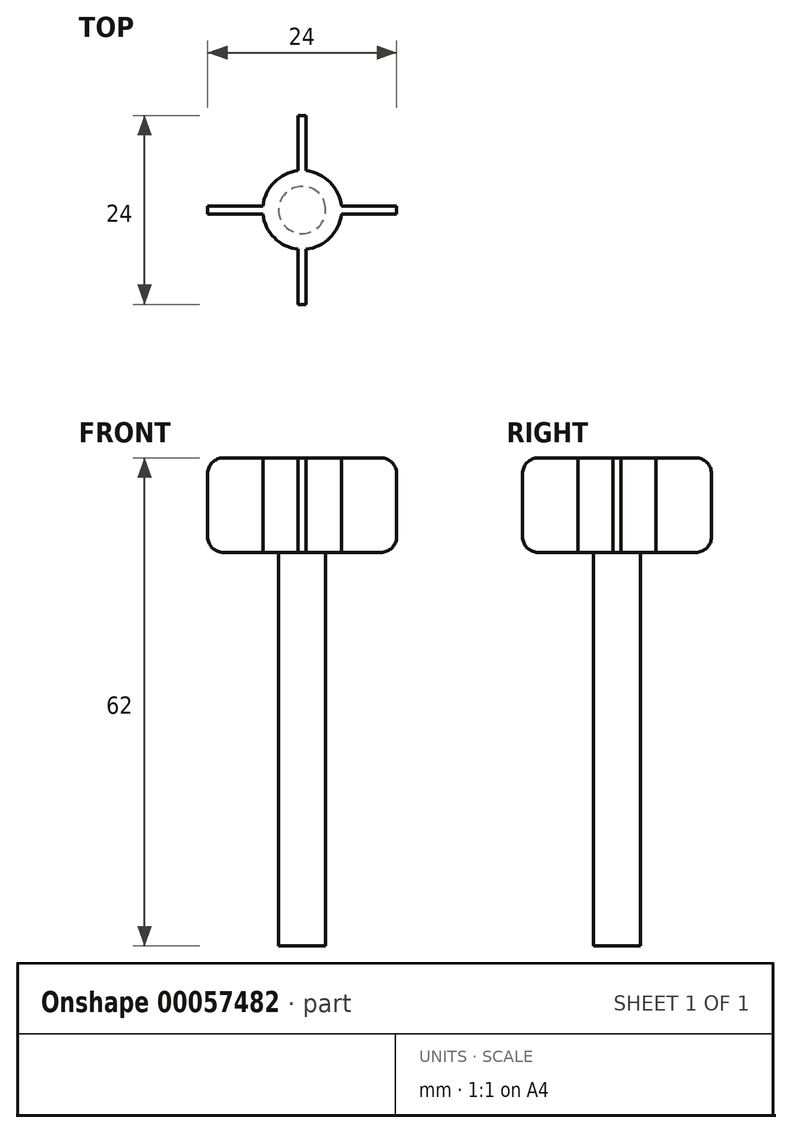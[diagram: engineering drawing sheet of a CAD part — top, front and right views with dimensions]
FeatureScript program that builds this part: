
annotation { "Feature Type Name" : "Feature", "Feature Type Description" : "" }
export const myFeature = defineFeature(function(context is Context, id is Id, definition is map)
    precondition{}
    {
        {
            var Q0;
            Q0=qCreatedBy(makeId("Top.planeOp"),FACE);
            var sketch = newSketch(context, id + "F0", { "sketchPlane" : qUnion([Q0])});
            skArc(sketch, "E0", {"start": v(-0.5, 4.97) * mm, "mid": v(-3.54, 3.54) * mm, "end": v(-4.97, 0.5) * mm});
            skLineSegment(sketch, "E1.bottom", {"start": v(12, 0.5) * mm, "end": v(4.97, 0.5) * mm});
            skLineSegment(sketch, "E1.top", {"start": v(12, -0.5) * mm, "end": v(4.97, -0.5) * mm});
            skLineSegment(sketch, "E1.left", {"start": v(12, 0.5) * mm, "end": v(12, -0.5) * mm});
            skLineSegment(sketch, "E1.right", {"start": v(-12, 0.5) * mm, "end": v(-12, -0.5) * mm});
            skLineSegment(sketch, "E2.bottom", {"start": v(0.5, 12) * mm, "end": v(-0.5, 12) * mm});
            skLineSegment(sketch, "E2.top", {"start": v(0.5, -12) * mm, "end": v(-0.5, -12) * mm});
            skLineSegment(sketch, "E2.left", {"start": v(0.5, 12) * mm, "end": v(0.5, 4.97) * mm});
            skLineSegment(sketch, "E2.right", {"start": v(-0.5, 12) * mm, "end": v(-0.5, 4.97) * mm});
            skArc(sketch, "E3.trimOffspring", {"start": v(4.97, 0.5) * mm, "mid": v(3.54, 3.54) * mm, "end": v(0.5, 4.97) * mm});
            skLineSegment(sketch, "E4.trimOffspring", {"start": v(-4.97, 0.5) * mm, "end": v(-12, 0.5) * mm});
            skLineSegment(sketch, "E5.trimOffspring", {"start": v(-4.97, -0.5) * mm, "end": v(-12, -0.5) * mm});
            skArc(sketch, "E6.trimOffspring", {"start": v(-4.97, -0.5) * mm, "mid": v(-3.54, -3.54) * mm, "end": v(-0.5, -4.97) * mm});
            skArc(sketch, "E7.trimOffspring", {"start": v(0.5, -4.97) * mm, "mid": v(3.54, -3.54) * mm, "end": v(4.97, -0.5) * mm});
            skLineSegment(sketch, "E8.trimOffspring", {"start": v(0.5, -4.97) * mm, "end": v(0.5, -12) * mm});
            skLineSegment(sketch, "E9.trimOffspring", {"start": v(-0.5, -4.97) * mm, "end": v(-0.5, -12) * mm});
            skSolve(sketch);
        }
        {
            var Q0;
            Q0=makeQuery(id+"F0.imprint","IMPRINT",FACE,{"disambiguationData":[TD([[makeQuery(id+"F0.imprint","IMPRINT",EDGE,{"derivedFrom":sQuery(id+"F0.wireOp",EDGE,"E0")}),1.0]])]});
            extrude(context, id + "F1", {"entities" : qUnion([Q0]), "depth" : 12 * mm});
        }
        {
            var Q0;
            Q0=makeQuery(id+"F1.opExtrude","CAP_EDGE",EDGE,{"disambiguationData":[OSD([sQuery(id+"F0.wireOp",EDGE,"E1.right")])],"isStart":false});
            var Q1;
            Q1=makeQuery(id+"F1.opExtrude","CAP_EDGE",EDGE,{"disambiguationData":[OSD([sQuery(id+"F0.wireOp",EDGE,"E1.right")])],"isStart":true});
            var Q2;
            Q2=makeQuery(id+"F1.opExtrude","CAP_EDGE",EDGE,{"disambiguationData":[OSD([sQuery(id+"F0.wireOp",EDGE,"E2.bottom")])],"isStart":false});
            var Q3;
            Q3=makeQuery(id+"F1.opExtrude","CAP_EDGE",EDGE,{"disambiguationData":[OSD([sQuery(id+"F0.wireOp",EDGE,"E1.left")])],"isStart":false});
            var Q4;
            Q4=makeQuery(id+"F1.opExtrude","CAP_EDGE",EDGE,{"disambiguationData":[OSD([sQuery(id+"F0.wireOp",EDGE,"E2.top")])],"isStart":false});
            var Q5;
            Q5=makeQuery(id+"F1.opExtrude","CAP_EDGE",EDGE,{"disambiguationData":[OSD([sQuery(id+"F0.wireOp",EDGE,"E2.bottom")])],"isStart":true});
            var Q6;
            Q6=makeQuery(id+"F1.opExtrude","CAP_EDGE",EDGE,{"disambiguationData":[OSD([sQuery(id+"F0.wireOp",EDGE,"E1.left")])],"isStart":true});
            var Q7;
            Q7=makeQuery(id+"F1.opExtrude","CAP_EDGE",EDGE,{"disambiguationData":[OSD([sQuery(id+"F0.wireOp",EDGE,"E2.top")])],"isStart":true});
            fillet(context, id + "F2", {"entities" : qUnion([Q0, Q1, Q2, Q3, Q4, Q5, Q6, Q7]), "radius" : 2 * mm, "tangentPropagation" : true, "allowEdgeOverflow" : false});
        }
        {
            var Q0;
            Q0=makeQuery(id+"F1.opExtrude","CAP_FACE",FACE,{"disambiguationData":[OSD([sQuery(id+"F0.wireOp",EDGE,"E0"),sQuery(id+"F0.wireOp",EDGE,"E1.bottom"),sQuery(id+"F0.wireOp",EDGE,"E1.top"),sQuery(id+"F0.wireOp",EDGE,"E1.left"),sQuery(id+"F0.wireOp",EDGE,"E1.right"),sQuery(id+"F0.wireOp",EDGE,"E2.bottom"),sQuery(id+"F0.wireOp",EDGE,"E2.top"),sQuery(id+"F0.wireOp",EDGE,"E2.left"),sQuery(id+"F0.wireOp",EDGE,"E2.right"),sQuery(id+"F0.wireOp",EDGE,"E3.trimOffspring"),sQuery(id+"F0.wireOp",EDGE,"E4.trimOffspring"),sQuery(id+"F0.wireOp",EDGE,"E5.trimOffspring"),sQuery(id+"F0.wireOp",EDGE,"E6.trimOffspring"),sQuery(id+"F0.wireOp",EDGE,"E7.trimOffspring"),sQuery(id+"F0.wireOp",EDGE,"E8.trimOffspring"),sQuery(id+"F0.wireOp",EDGE,"E9.trimOffspring")])],"isStart":true});
            var sketch = newSketch(context, id + "F3", { "sketchPlane" : qUnion([Q0])});
            skCircle(sketch, "E10", {"center": v(0, 0) * mm, "radius": 3 * mm});
            skSolve(sketch);
        }
        {
            var Q0;
            Q0=makeQuery(id+"F3.imprint","IMPRINT",FACE,{"disambiguationData":[TD([[makeQuery(id+"F3.imprint","IMPRINT",EDGE,{"derivedFrom":sQuery(id+"F3.wireOp",EDGE,"E10")}),1.0]])]});
            extrude(context, id + "F4", {"entities" : qUnion([Q0]), "operationType" : NewBodyOperationType.ADD, "depth" : 50 * mm});
        }
    });
